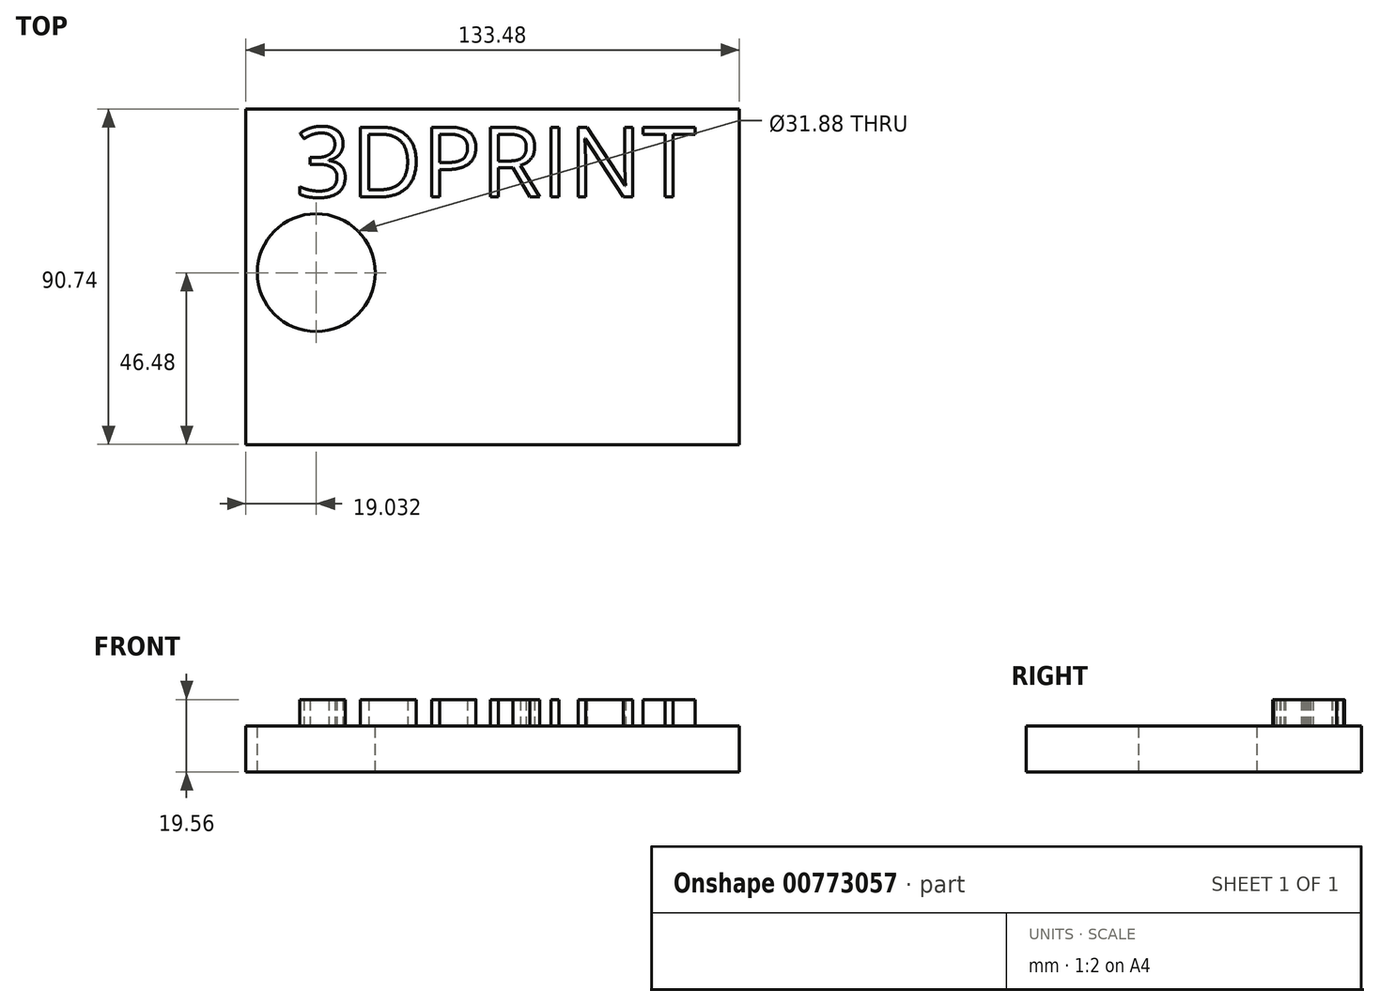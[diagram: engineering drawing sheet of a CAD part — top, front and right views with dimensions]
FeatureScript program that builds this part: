
annotation { "Feature Type Name" : "Feature", "Feature Type Description" : "" }
export const myFeature = defineFeature(function(context is Context, id is Id, definition is map)
    precondition{}
    {
        {
            var Q0;
            Q0=qCreatedBy(makeId("Top.planeOp"),FACE);
            var sketch = newSketch(context, id + "F0", { "sketchPlane" : qUnion([Q0])});
            skLineSegment(sketch, "E0.bottom", {"start": v(-68.67, 44.26) * mm, "end": v(64.81, 44.26) * mm});
            skLineSegment(sketch, "E0.top", {"start": v(-68.67, -46.48) * mm, "end": v(64.81, -46.48) * mm});
            skLineSegment(sketch, "E0.left", {"start": v(-68.67, 44.26) * mm, "end": v(-68.67, -46.48) * mm});
            skLineSegment(sketch, "E0.right", {"start": v(64.81, 44.26) * mm, "end": v(64.81, -46.48) * mm});
            skSolve(sketch);
        }
        {
            var Q0;
            Q0=makeQuery(id+"F0.imprint","IMPRINT",FACE,{"disambiguationData":[TD([[makeQuery(id+"F0.imprint","IMPRINT",EDGE,{"derivedFrom":sQuery(id+"F0.wireOp",EDGE,"E0.bottom")}),-1.0]])]});
            extrude(context, id + "F1", {"entities" : qUnion([Q0]), "depth" : 12.45 * mm, "offsetDistance" : 25.4 * mm});
        }
        {
            var Q0;
            Q0=makeQuery(id+"F1.opExtrude","CAP_FACE",FACE,{"disambiguationData":[OSD([sQuery(id+"F0.wireOp",EDGE,"E0.bottom"),sQuery(id+"F0.wireOp",EDGE,"E0.top"),sQuery(id+"F0.wireOp",EDGE,"E0.left"),sQuery(id+"F0.wireOp",EDGE,"E0.right")])],"isStart":false});
            var sketch = newSketch(context, id + "F2", { "sketchPlane" : qUnion([Q0])});
            skCircle(sketch, "E1", {"center": v(-49.64, 0) * mm, "radius": 16.04 * mm});
            skCircle(sketch, "E2", {"center": v(-49.64, 0) * mm, "radius": 15.94 * mm});
            skSolve(sketch);
        }
        {
            var Q0;
            Q0=makeQuery(id+"F2.imprint","IMPRINT",FACE,{"disambiguationData":[TD([[makeQuery(id+"F2.imprint","IMPRINT",EDGE,{"derivedFrom":sQuery(id+"F2.wireOp",EDGE,"E2")}),1.0]])]});
            extrude(context, id + "F3", {"entities" : qUnion([Q0]), "operationType" : NewBodyOperationType.REMOVE, "oppositeDirection" : true, "depth" : 40.9 * mm, "offsetDistance" : 25.4 * mm});
        }
        {
            var Q0;
            Q0=makeQuery(id+"F1.opExtrude","CAP_FACE",FACE,{"disambiguationData":[OSD([sQuery(id+"F0.wireOp",EDGE,"E0.bottom"),sQuery(id+"F0.wireOp",EDGE,"E0.top"),sQuery(id+"F0.wireOp",EDGE,"E0.left"),sQuery(id+"F0.wireOp",EDGE,"E0.right")])],"isStart":false});
            var sketch = newSketch(context, id + "F4", { "sketchPlane" : qUnion([Q0])});
            skText(sketch, "E3", { "text": "3DPRINT", "fontName": "OpenSans-Regular.ttf"});
            const initialGuessF4  = {"E3": [-0.05535, 0.0205, 1, 0, 0.01901]};
            skSetInitialGuess(sketch, initialGuessF4);
            skSolve(sketch);
        }
        {
            var Q0;
            Q0 = qSketchRegion(id + "F4", true);
            extrude(context, id + "F5", {"entities" : qUnion([Q0]), "operationType" : NewBodyOperationType.ADD, "depth" : 7.11 * mm, "offsetDistance" : 25.4 * mm});
        }
    });
